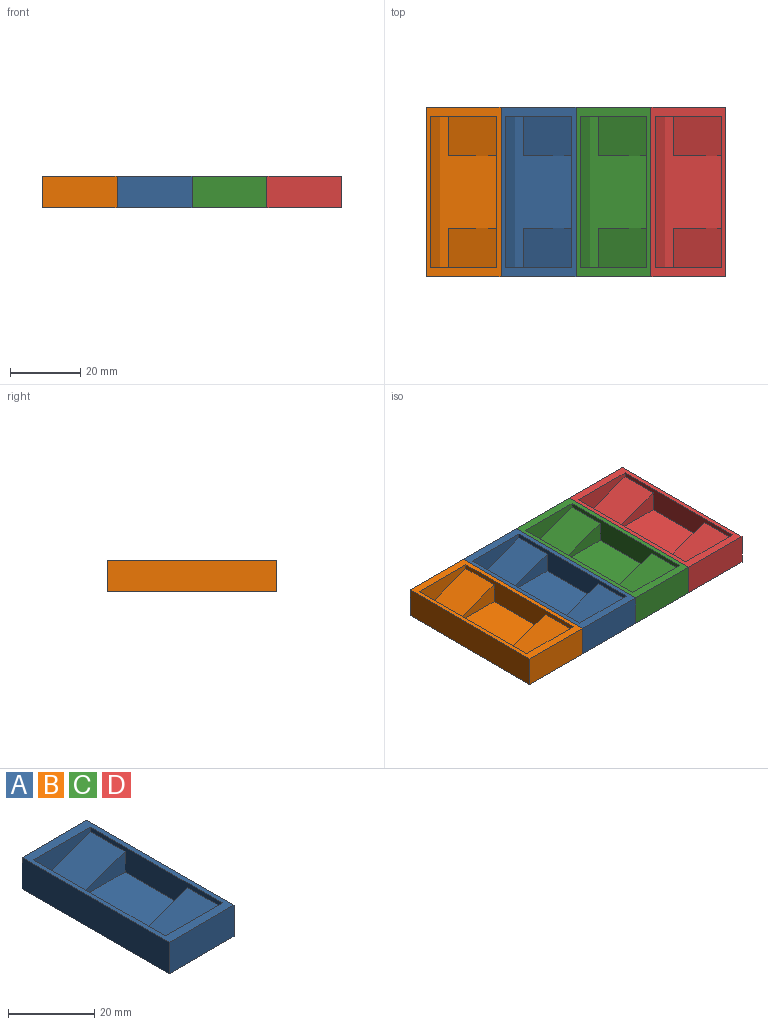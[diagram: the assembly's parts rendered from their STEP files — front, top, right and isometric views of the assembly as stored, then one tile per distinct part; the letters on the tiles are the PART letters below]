
ASSEMBLY  parts=4 mates=9
PART A: 17 faces, bbox 21.3x48.3x8.9 mm
  f0: plane 11.3x0.92mm, normal (-1,0,0), area 10.4mm2, adj f10,f12,f14,f16
  f1: plane 13.57x11.3mm, normal (-0.34,0,0.94), area 163.2mm2, adj f8,f11,f13,f15
  f2: plane 48.26x21.34mm, normal (0,0,1), area 221.5mm2, adj f3,f5,f6,f7,f8,f9,f13,f14
  f3: plane 48.26x8.89mm, normal (-1,0,0), area 429mm2, adj f2,f4,f6,f7
  f4: plane 48.26x21.34mm, normal (0,0,-1), area 1029.7mm2, adj f3,f5,f6,f7
  f5: plane 48.26x8.89mm, normal (1,0,0), area 429mm2, adj f2,f4,f6,f7
  f6: plane 21.34x8.89mm, normal (0,-1,0), area 189.7mm2, adj f2,f3,f4,f5
  f7: plane 21.34x8.89mm, normal (0,1,0), area 189.7mm2, adj f2,f3,f4,f5
  f8: plane 43.18x7.16mm, normal (-1,0,0), area 176.6mm2, adj f1,f2,f10,f12,f13,f14,f15,f16
  f9: plane 43.18x7.16mm, normal (0.94,0,0.34), area 329mm2, adj f2,f10,f13,f14
  f10: plane 43.18x16.11mm, normal (0,0,1), area 388.9mm2, adj f0,f8,f9,f11,f13,f14,f15,f16
  f11: plane 11.3x0.92mm, normal (-1,0,0), area 10.4mm2, adj f1,f10,f13,f15
  f12: plane 13.57x11.3mm, normal (-0.34,0,0.94), area 163.2mm2, adj f0,f8,f14,f16
  f13: plane 18.72x7.16mm, normal (0,-1,0), area 78.6mm2, adj f1,f2,f8,f9,f10,f11
  f14: plane 18.72x7.16mm, normal (0,1,0), area 78.6mm2, adj f0,f2,f8,f9,f10,f12
  f15: plane 13.57x5.86mm, normal (0,-1,0), area 46.1mm2, adj f1,f8,f10,f11
  f16: plane 13.57x5.86mm, normal (0,1,0), area 46.1mm2, adj f0,f8,f10,f12
PART B: same geometry as A
PART C: same geometry as A
PART D: same geometry as A
PLACE A t=(-38.02,-0.74,9.83)mm
PLACE B t=(-59.35,-0.74,9.83)mm
PLACE C t=(-16.68,-0.74,9.83)mm
PLACE D t=(4.65,-0.74,9.83)mm
MATE planar A.f4 <-> D.f4  axis (0,0,-1) through (-27.35,-0.74,9.83)mm
MATE planar C.f5 <-> D.f3  axis (1,0,0) through (4.65,-0.74,14.28)mm
MATE planar A.f4 <-> C.f4  axis (0,0,-1) through (-27.35,-0.74,9.83)mm
MATE planar A.f4 <-> B.f4  axis (0,0,-1) through (-27.35,-0.74,9.83)mm
MATE planar B.f5 <-> A.f3  axis (1,0,0) through (-38.02,-0.74,14.28)mm
MATE planar A.f5 <-> C.f3  axis (1,0,0) through (-16.68,-0.74,14.28)mm
MATE planar B.f6 <-> D.f6  axis (0,-1,0) through (-48.69,-24.87,14.28)mm
MATE planar C.f6 <-> D.f6  axis (0,-1,0) through (-6.01,-24.87,14.28)mm
MATE planar D.f6 <-> A.f6  axis (0,-1,0) through (15.32,-24.87,14.28)mm
